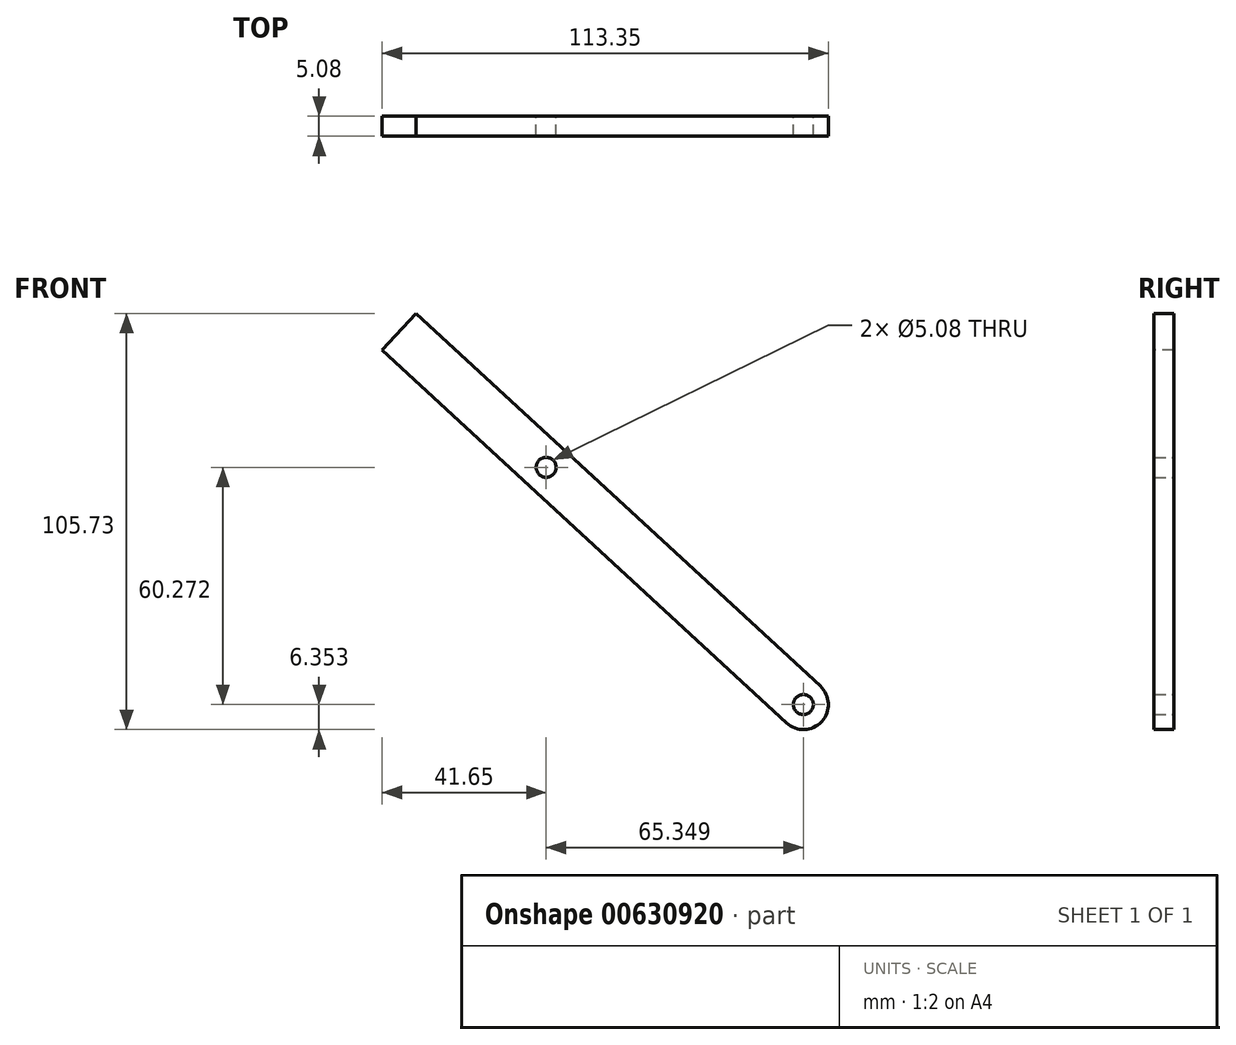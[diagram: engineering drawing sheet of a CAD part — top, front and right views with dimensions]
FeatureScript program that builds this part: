
annotation { "Feature Type Name" : "Feature", "Feature Type Description" : "" }
export const myFeature = defineFeature(function(context is Context, id is Id, definition is map)
    precondition{}
    {
        {
            var Q0;
            Q0=qCreatedBy(makeId("Front.planeOp"),FACE);
            var sketch = newSketch(context, id + "F0", { "sketchPlane" : qUnion([Q0])});
            skCircle(sketch, "E0", {"center": v(-25.86, -42) * mm, "radius": 6.35 * mm});
            skCircle(sketch, "E1", {"center": v(-91.21, 18.28) * mm, "radius": 6.35 * mm});
            skLineSegment(sketch, "E2", {"start": v(-86.9, 22.94) * mm, "end": v(-21.56, -37.33) * mm});
            skLineSegment(sketch, "E3", {"start": v(-95.52, 13.6) * mm, "end": v(-30.17, -46.66) * mm});
            skCircle(sketch, "E4", {"center": v(-91.21, 18.28) * mm, "radius": 2.54 * mm});
            skCircle(sketch, "E5", {"center": v(-25.86, -42) * mm, "radius": 2.54 * mm});
            skSolve(sketch);
        }
        {
            var Q0;
            Q0 = qSketchRegion(id + "F0", true);
            extrude(context, id + "F1", {"entities" : qUnion([Q0]), "depth" : 5.08 * mm, "offsetDistance" : 25.4 * mm});
        }
        {
            var Q0;
            Q0=makeQuery(id+"F1.opExtrude","CAP_FACE",FACE,{"disambiguationData":[OSD([sQuery(id+"F0.wireOp",EDGE,"E0"),sQuery(id+"F0.wireOp",EDGE,"E1"),sQuery(id+"F0.wireOp",EDGE,"E2"),sQuery(id+"F0.wireOp",EDGE,"E3"),sQuery(id+"F0.wireOp",EDGE,"E4"),sQuery(id+"F0.wireOp",EDGE,"E5")])],"isStart":false});
            var sketch = newSketch(context, id + "F2", { "sketchPlane" : qUnion([Q0])});
            skLineSegment(sketch, "E6", {"start": v(-86.9, 22.94) * mm, "end": v(-124.25, 57.38) * mm});
            skLineSegment(sketch, "E7", {"start": v(-95.52, 13.6) * mm, "end": v(-132.86, 48.05) * mm});
            skLineSegment(sketch, "E8", {"start": v(-132.86, 48.05) * mm, "end": v(-124.25, 57.38) * mm});
            skSolve(sketch);
        }
        {
            var Q0;
            Q0 = qSketchRegion(id + "F2", true);
            var Q1;
            Q1=makeQuery(id+"F2.imprint","IMPRINT",FACE,{"disambiguationData":[TD([[makeQuery(id+"F2.imprint","IMPRINT",EDGE,{"derivedFrom":sQuery(id+"F2.wireOp",EDGE,"E6")}),1.0]])]});
            extrude(context, id + "F3", {"entities" : qUnion([Q0, Q1]), "operationType" : NewBodyOperationType.ADD, "oppositeDirection" : true, "depth" : 5.08 * mm, "offsetDistance" : 25.4 * mm});
        }
    });
